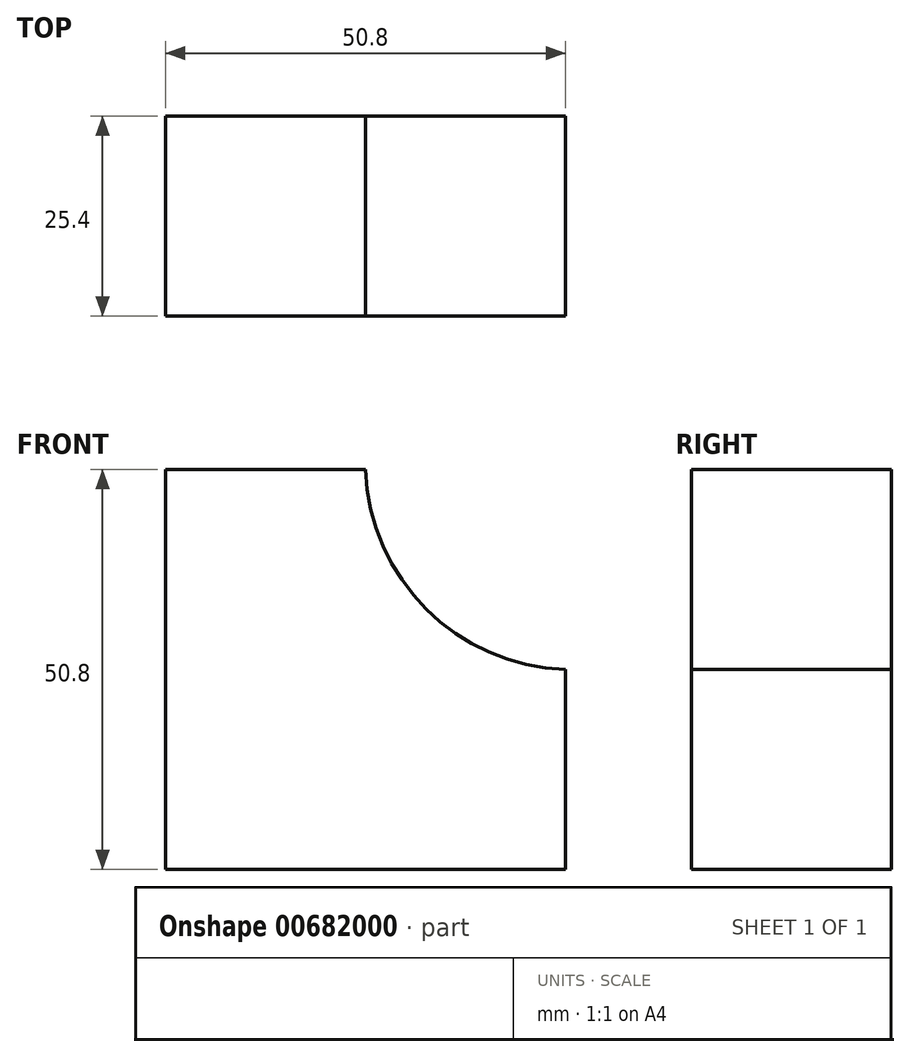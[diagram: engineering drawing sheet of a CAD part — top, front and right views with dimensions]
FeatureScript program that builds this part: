
annotation { "Feature Type Name" : "Feature", "Feature Type Description" : "" }
export const myFeature = defineFeature(function(context is Context, id is Id, definition is map)
    precondition{}
    {
        {
            var Q0;
            Q0=qCreatedBy(makeId("Front.planeOp"),FACE);
            var sketch = newSketch(context, id + "F0", { "sketchPlane" : qUnion([Q0])});
            skLineSegment(sketch, "E0", {"start": v(0, 0) * mm, "end": v(-50.8, 0) * mm});
            skLineSegment(sketch, "E1", {"start": v(-50.8, 0) * mm, "end": v(-50.8, 50.8) * mm});
            skLineSegment(sketch, "E2", {"start": v(-50.8, 50.8) * mm, "end": v(-25.4, 50.8) * mm});
            skLineSegment(sketch, "E3", {"start": v(0, 0) * mm, "end": v(0, 25.4) * mm});
            skArc(sketch, "E4", {"start": v(-25.4, 50.8) * mm, "mid": v(-17.7, 33.1) * mm, "end": v(0, 25.4) * mm});
            skSolve(sketch);
        }
        {
            var Q0;
            Q0=makeQuery(id+"F0.imprint","IMPRINT",FACE,{"disambiguationData":[TD([[makeQuery(id+"F0.imprint","IMPRINT",EDGE,{"derivedFrom":sQuery(id+"F0.wireOp",EDGE,"E0")}),-1.0]])]});
            extrude(context, id + "F1", {"entities" : qUnion([Q0]), "depth" : 25.4 * mm, "offsetDistance" : 25.4 * mm});
        }
    });
